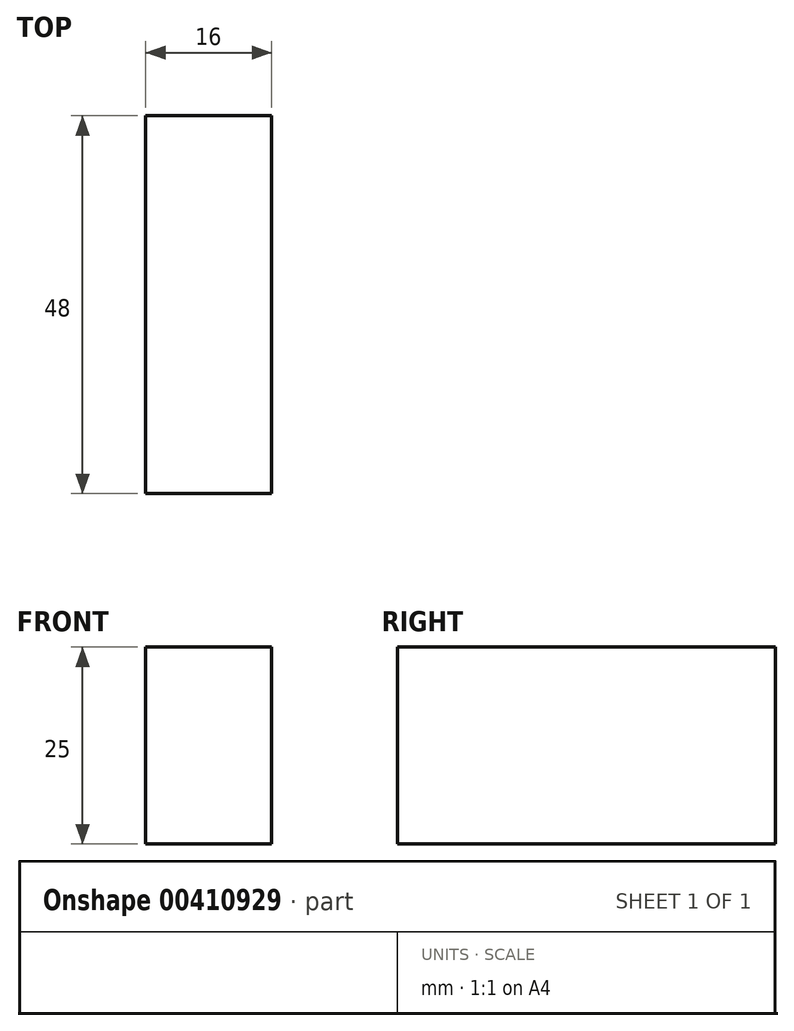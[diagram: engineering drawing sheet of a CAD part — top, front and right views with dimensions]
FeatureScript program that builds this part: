
annotation { "Feature Type Name" : "Feature", "Feature Type Description" : "" }
export const myFeature = defineFeature(function(context is Context, id is Id, definition is map)
    precondition{}
    {
        {
            var Q0;
            Q0=qCreatedBy(makeId("Top.planeOp"),FACE);
            var sketch = newSketch(context, id + "F0", { "sketchPlane" : qUnion([Q0])});
            skLineSegment(sketch, "E0.bottom", {"start": v(0, 0) * mm, "end": v(16, 0) * mm});
            skLineSegment(sketch, "E0.top", {"start": v(0, 48) * mm, "end": v(16, 48) * mm});
            skLineSegment(sketch, "E0.left", {"start": v(0, 0) * mm, "end": v(0, 48) * mm});
            skLineSegment(sketch, "E0.right", {"start": v(16, 0) * mm, "end": v(16, 48) * mm});
            skSolve(sketch);
        }
        {
            var Q0;
            Q0 = qSketchRegion(id + "F0", true);
            extrude(context, id + "F1", {"entities" : qUnion([Q0]), "depth" : 25 * mm});
        }
    });
